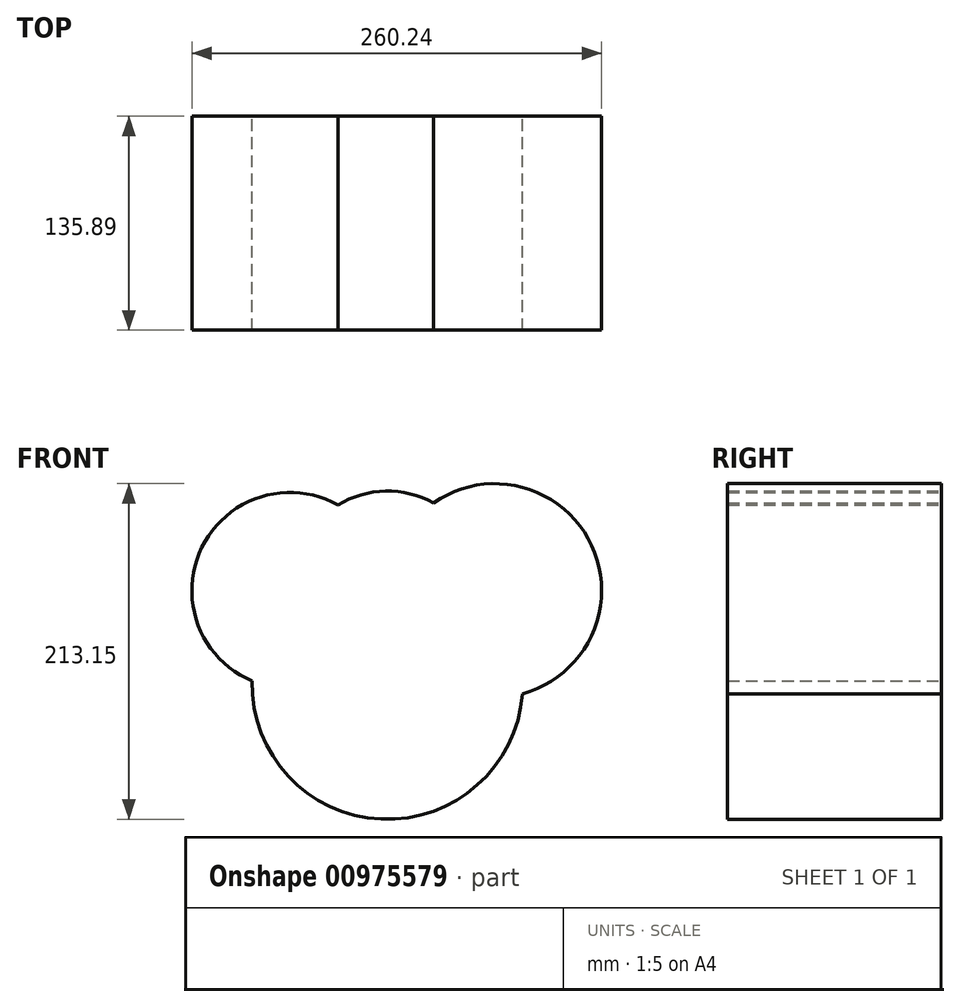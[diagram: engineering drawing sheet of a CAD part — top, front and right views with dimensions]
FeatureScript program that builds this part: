
annotation { "Feature Type Name" : "Feature", "Feature Type Description" : "" }
export const myFeature = defineFeature(function(context is Context, id is Id, definition is map)
    precondition{}
    {
        {
            var Q0;
            Q0=qCreatedBy(makeId("Front.planeOp"),FACE);
            var sketch = newSketch(context, id + "F0", { "sketchPlane" : qUnion([Q0])});
            skCircle(sketch, "E0", {"center": v(-62.28, 0) * mm, "radius": 62.28 * mm});
            skCircle(sketch, "E1", {"center": v(67.84, 0) * mm, "radius": 67.84 * mm});
            skArc(sketch, "E2", {"start": v(-28.6, -52.4) * mm, "mid": v(-14.92, -57.57) * mm, "end": v(-0.4, -59.35) * mm});
            skArc(sketch, "E3", {"start": v(5.35, 26.41) * mm, "mid": v(-0.27, 26.6) * mm, "end": v(-5.89, 26.43) * mm});
            skArc(sketch, "E4", {"start": v(-0.4, -145.3) * mm, "mid": v(20.98, -102.33) * mm, "end": v(-0.4, -59.35) * mm});
            skArc(sketch, "E5.trimOffspring", {"start": v(29.03, 55.64) * mm, "mid": v(-1.58, 63.09) * mm, "end": v(-31.83, 54.33) * mm});
            skArc(sketch, "E6.trimOffspring", {"start": v(-61.48, 1.13) * mm, "mid": v(-0.6, -145.3) * mm, "end": v(60.96, 0.85) * mm});
            skLineSegment(sketch, "E7", {"start": v(-32.9, -102.33) * mm, "end": v(-0.4, -145.3) * mm});
            skSolve(sketch);
        }
        {
            var Q0;
            {var subQ0=sQuery(id+"F0.wireOp",EDGE,"E2");Q0=makeQuery(id+"F0.imprint","IMPRINT",FACE,{"disambiguationData":[TD([[makeQuery(id+"F0.imprint","IMPRINT",EDGE,{"derivedFrom":subQ0}),-1.0]])]});}
            var Q1;
            {var subQ0=sQuery(id+"F0.wireOp",EDGE,"E1");var subQ1=makeQuery(id+"F0.imprint","INTERSECT",VERTEX,{"derivedFrom":[subQ0,sQuery(id+"F0.wireOp",EDGE,"E3")]});Q1=makeQuery(id+"F0.imprint","IMPRINT",FACE,{"disambiguationData":[TD([[makeQuery(id+"F0.imprint","IMPRINT",EDGE,{"disambiguationData":[TD([[subQ1,1.0]])],"derivedFrom":subQ0}),1.0]])]});}
            var Q2;
            {var subQ0=sQuery(id+"F0.wireOp",EDGE,"E3");Q2=makeQuery(id+"F0.imprint","IMPRINT",FACE,{"disambiguationData":[TD([[makeQuery(id+"F0.imprint","IMPRINT",EDGE,{"derivedFrom":subQ0}),-1.0]])]});}
            var Q3;
            {var subQ0=sQuery(id+"F0.wireOp",EDGE,"E0");var subQ4=makeQuery(id+"F0.imprint","INTERSECT",VERTEX,{"derivedFrom":[subQ0,sQuery(id+"F0.wireOp",EDGE,"E3")]});Q3=makeQuery(id+"F0.imprint","IMPRINT",FACE,{"disambiguationData":[TD([[makeQuery(id+"F0.imprint","IMPRINT",EDGE,{"disambiguationData":[TD([[subQ4,1.0]])],"derivedFrom":subQ0}),1.0]])]});}
            var Q4;
            {var subQ6=sQuery(id+"F0.wireOp",EDGE,"E2");Q4=makeQuery(id+"F0.imprint","IMPRINT",FACE,{"disambiguationData":[TD([[makeQuery(id+"F0.imprint","IMPRINT",EDGE,{"derivedFrom":subQ6}),1.0]])]});}
            var Q5;
            {var subQ0=sQuery(id+"F0.wireOp",EDGE,"E3");Q5=makeQuery(id+"F0.imprint","IMPRINT",FACE,{"disambiguationData":[TD([[makeQuery(id+"F0.imprint","IMPRINT",EDGE,{"derivedFrom":subQ0}),1.0]])]});}
            extrude(context, id + "F1", {"entities" : qUnion([Q0, Q1, Q2, Q3, Q4, Q5]), "depth" : 135.89 * mm, "offsetDistance" : 25.4 * mm});
        }
    });
